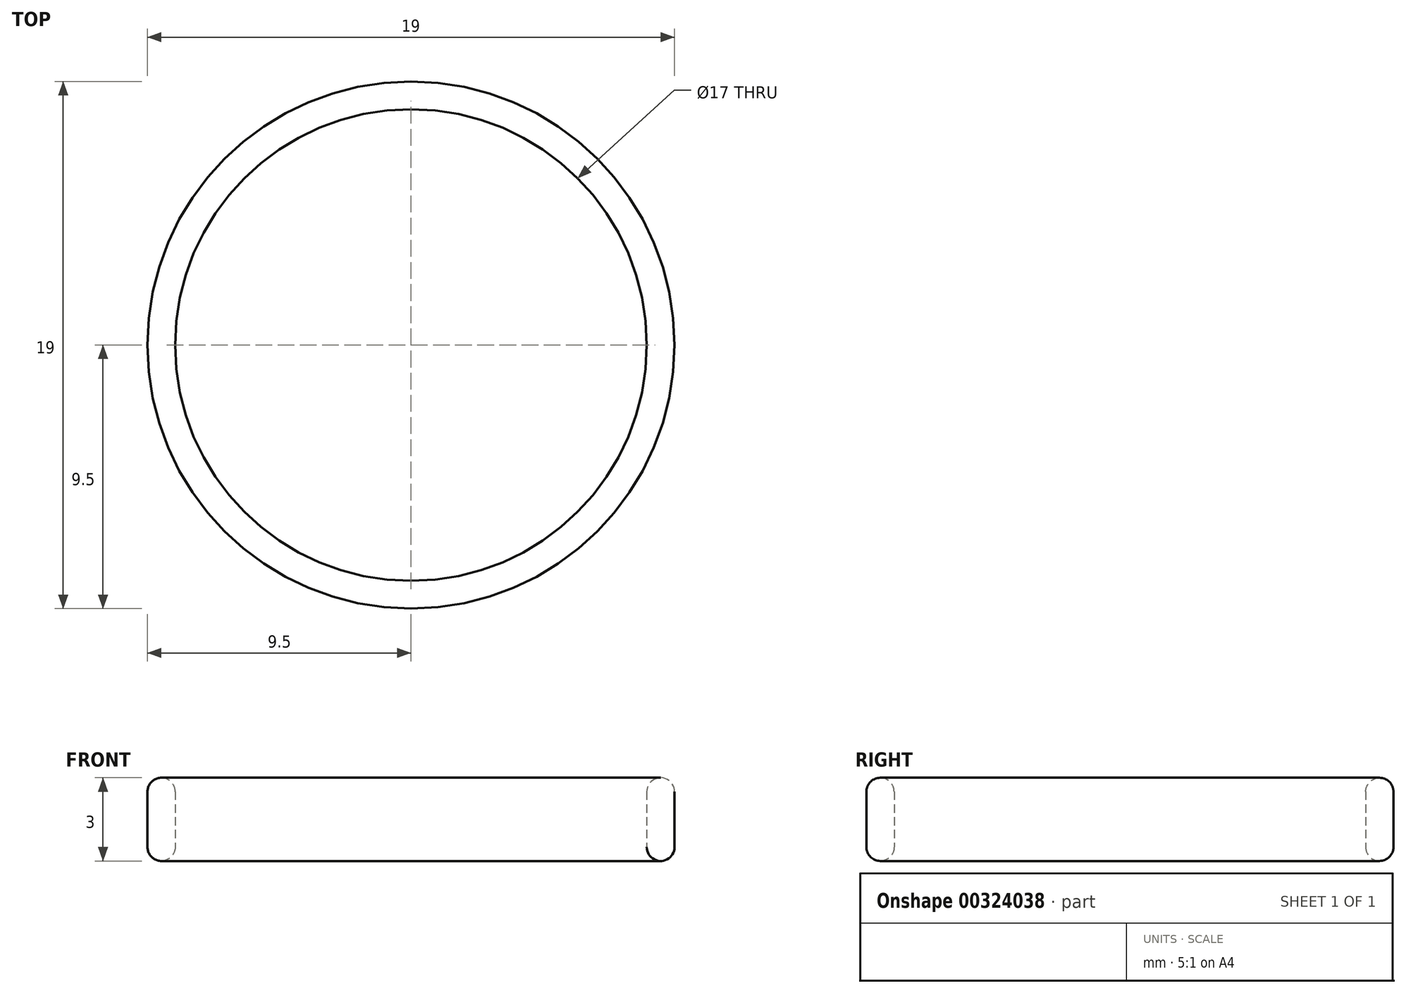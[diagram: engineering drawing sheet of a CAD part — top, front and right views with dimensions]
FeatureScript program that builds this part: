
annotation { "Feature Type Name" : "Feature", "Feature Type Description" : "" }
export const myFeature = defineFeature(function(context is Context, id is Id, definition is map)
    precondition{}
    {
        {
            var Q0;
            Q0=qCreatedBy(makeId("Top.planeOp"),FACE);
            var sketch = newSketch(context, id + "F0", { "sketchPlane" : qUnion([Q0])});
            skCircle(sketch, "E0", {"center": v(0, 0) * mm, "radius": 8.5 * mm});
            skCircle(sketch, "E1", {"center": v(0, 0) * mm, "radius": 9.5 * mm});
            skSolve(sketch);
        }
        {
            var Q0;
            Q0=makeQuery(id+"F0.imprint","IMPRINT",FACE,{"disambiguationData":[TD([[makeQuery(id+"F0.imprint","IMPRINT",EDGE,{"derivedFrom":sQuery(id+"F0.wireOp",EDGE,"E0")}),-1.0]])]});
            extrude(context, id + "F1", {"entities" : qUnion([Q0]), "depth" : 3 * mm});
        }
        {
            var Q0;
            Q0=makeQuery(id+"F1.opExtrude","CAP_EDGE",EDGE,{"disambiguationData":[OSD([sQuery(id+"F0.wireOp",EDGE,"E1")])],"isStart":false});
            var Q1;
            Q1=makeQuery(id+"F1.opExtrude","CAP_EDGE",EDGE,{"disambiguationData":[OSD([sQuery(id+"F0.wireOp",EDGE,"E0")])],"isStart":false});
            var Q2;
            Q2=makeQuery(id+"F1.opExtrude","CAP_EDGE",EDGE,{"disambiguationData":[OSD([sQuery(id+"F0.wireOp",EDGE,"E1")])],"isStart":true});
            var Q3;
            Q3=makeQuery(id+"F1.opExtrude","CAP_EDGE",EDGE,{"disambiguationData":[OSD([sQuery(id+"F0.wireOp",EDGE,"E0")])],"isStart":true});
            fillet(context, id + "F2", {"entities" : qUnion([Q0, Q1, Q2, Q3]), "radius" : .5 * mm, "tangentPropagation" : true, "allowEdgeOverflow" : false});
        }
    });
